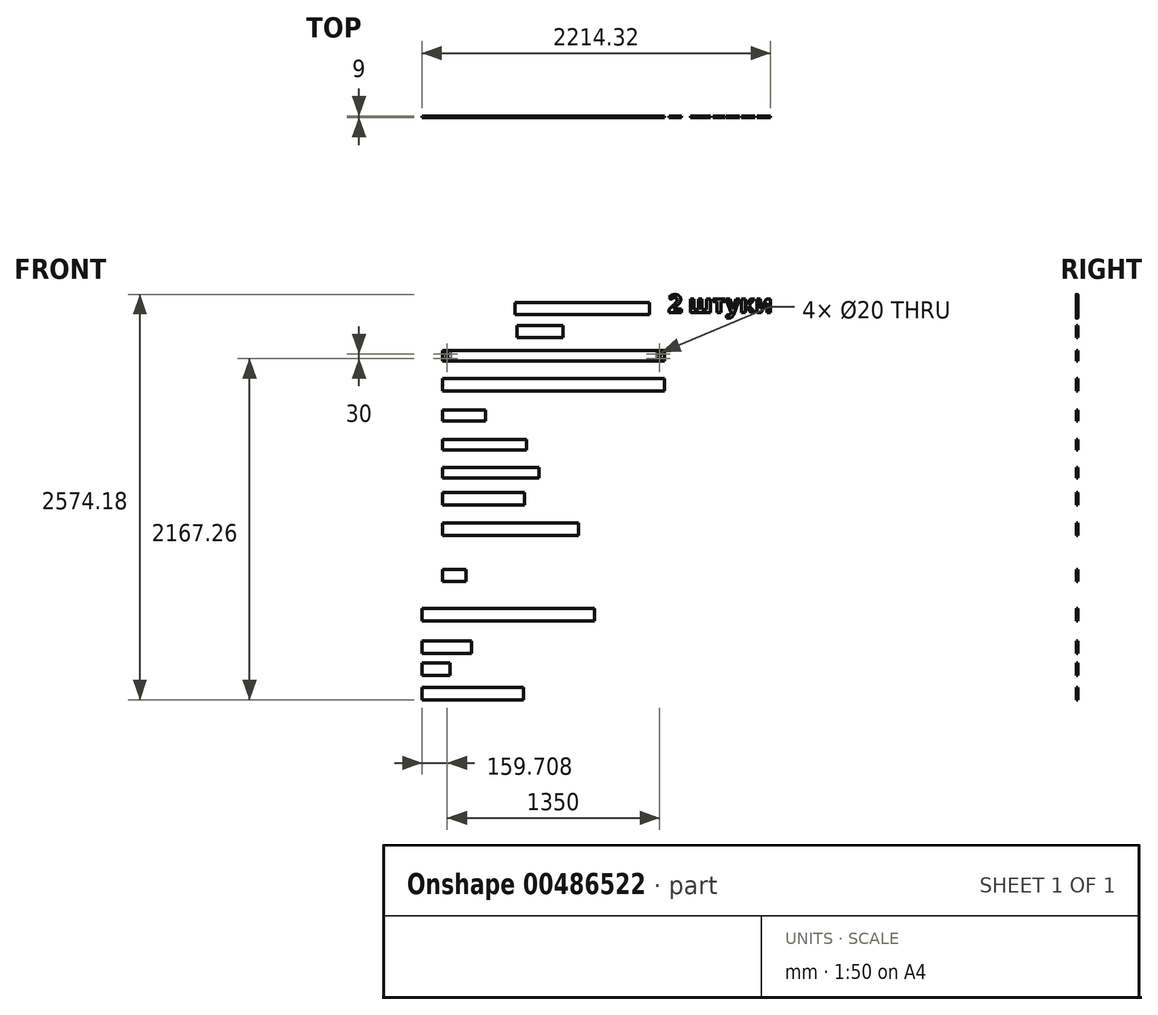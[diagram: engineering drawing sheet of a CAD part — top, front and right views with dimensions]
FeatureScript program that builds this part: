
annotation { "Feature Type Name" : "Feature", "Feature Type Description" : "" }
export const myFeature = defineFeature(function(context is Context, id is Id, definition is map)
    precondition{}
    {
        {
            var Q0;
            Q0=qCreatedBy(makeId("Front.planeOp"),FACE);
            var sketch = newSketch(context, id + "F0", { "sketchPlane" : qUnion([Q0])});
            skLineSegment(sketch, "E0.bottom", {"start": v(-789.19, 96.08) * mm, "end": v(63.81, 96.08) * mm});
            skLineSegment(sketch, "E0.top", {"start": v(-789.19, 18.08) * mm, "end": v(63.81, 18.08) * mm});
            skLineSegment(sketch, "E0.left", {"start": v(-789.19, 96.08) * mm, "end": v(-789.19, 18.08) * mm});
            skLineSegment(sketch, "E0.right", {"start": v(63.81, 96.08) * mm, "end": v(63.81, 18.08) * mm});
            skLineSegment(sketch, "E1.bottom", {"start": v(-776.91, -50.79) * mm, "end": v(-483.91, -50.79) * mm});
            skLineSegment(sketch, "E1.top", {"start": v(-776.91, -128.79) * mm, "end": v(-483.91, -128.79) * mm});
            skLineSegment(sketch, "E1.left", {"start": v(-776.91, -50.79) * mm, "end": v(-776.91, -128.79) * mm});
            skLineSegment(sketch, "E1.right", {"start": v(-483.91, -50.79) * mm, "end": v(-483.91, -128.79) * mm});
            skLineSegment(sketch, "E2.bottom", {"start": v(-1250.2, -211.61) * mm, "end": v(159.8, -211.61) * mm});
            skLineSegment(sketch, "E2.top", {"start": v(-1250.2, -276.61) * mm, "end": v(159.8, -276.61) * mm});
            skLineSegment(sketch, "E2.left", {"start": v(-1250.2, -211.61) * mm, "end": v(-1250.2, -276.61) * mm});
            skLineSegment(sketch, "E2.right", {"start": v(159.8, -211.61) * mm, "end": v(159.8, -276.61) * mm});
            skLineSegment(sketch, "E3.bottom", {"start": v(-1250.2, -388.95) * mm, "end": v(159.8, -388.95) * mm});
            skLineSegment(sketch, "E3.top", {"start": v(-1250.2, -465.95) * mm, "end": v(159.8, -465.95) * mm});
            skLineSegment(sketch, "E3.left", {"start": v(-1250.2, -388.95) * mm, "end": v(-1250.2, -465.95) * mm});
            skLineSegment(sketch, "E3.right", {"start": v(159.8, -388.95) * mm, "end": v(159.8, -465.95) * mm});
            skLineSegment(sketch, "E4", {"start": v(-1196.2, -211.61) * mm, "end": v(-1196.2, -276.61) * mm});
            skCircle(sketch, "E5", {"center": v(-1220.2, -231.61) * mm, "radius": 10 * mm});
            skCircle(sketch, "E6", {"center": v(-1220.2, -261.61) * mm, "radius": 10 * mm});
            skLineSegment(sketch, "E7", {"start": v(105.8, -211.61) * mm, "end": v(105.8, -276.61) * mm});
            skCircle(sketch, "E8", {"center": v(129.8, -231.61) * mm, "radius": 10 * mm});
            skCircle(sketch, "E9", {"center": v(129.8, -261.61) * mm, "radius": 10 * mm});
            skLineSegment(sketch, "E10.bottom", {"start": v(-1250.2, -589.65) * mm, "end": v(-975.2, -589.65) * mm});
            skLineSegment(sketch, "E10.top", {"start": v(-1250.2, -658.65) * mm, "end": v(-975.2, -658.65) * mm});
            skLineSegment(sketch, "E10.left", {"start": v(-1250.2, -589.65) * mm, "end": v(-1250.2, -658.65) * mm});
            skLineSegment(sketch, "E10.right", {"start": v(-975.2, -589.65) * mm, "end": v(-975.2, -658.65) * mm});
            skLineSegment(sketch, "E11.bottom", {"start": v(-1250.2, -774.1) * mm, "end": v(-715.2, -774.1) * mm});
            skLineSegment(sketch, "E11.top", {"start": v(-1250.2, -843.1) * mm, "end": v(-715.2, -843.1) * mm});
            skLineSegment(sketch, "E11.left", {"start": v(-1250.2, -774.1) * mm, "end": v(-1250.2, -843.1) * mm});
            skLineSegment(sketch, "E11.right", {"start": v(-715.2, -774.1) * mm, "end": v(-715.2, -843.1) * mm});
            skLineSegment(sketch, "E12.bottom", {"start": v(-1250.2, -951.78) * mm, "end": v(-637.2, -951.78) * mm});
            skLineSegment(sketch, "E12.top", {"start": v(-1250.2, -1020.78) * mm, "end": v(-637.2, -1020.78) * mm});
            skLineSegment(sketch, "E12.left", {"start": v(-1250.2, -951.78) * mm, "end": v(-1250.2, -1020.78) * mm});
            skLineSegment(sketch, "E12.right", {"start": v(-637.2, -951.78) * mm, "end": v(-637.2, -1020.78) * mm});
            skLineSegment(sketch, "E13.bottom", {"start": v(-1250.2, -1112.74) * mm, "end": v(-730.2, -1112.74) * mm});
            skLineSegment(sketch, "E13.top", {"start": v(-1250.2, -1190.74) * mm, "end": v(-730.2, -1190.74) * mm});
            skLineSegment(sketch, "E13.left", {"start": v(-1250.2, -1112.74) * mm, "end": v(-1250.2, -1190.74) * mm});
            skLineSegment(sketch, "E13.right", {"start": v(-730.2, -1112.74) * mm, "end": v(-730.2, -1190.74) * mm});
            skLineSegment(sketch, "E14.bottom", {"start": v(-1250.2, -1305.86) * mm, "end": v(-385.2, -1305.86) * mm});
            skLineSegment(sketch, "E14.top", {"start": v(-1250.2, -1383.86) * mm, "end": v(-385.2, -1383.86) * mm});
            skLineSegment(sketch, "E14.left", {"start": v(-1250.2, -1305.86) * mm, "end": v(-1250.2, -1383.86) * mm});
            skLineSegment(sketch, "E14.right", {"start": v(-385.2, -1305.86) * mm, "end": v(-385.2, -1383.86) * mm});
            skLineSegment(sketch, "E15.bottom", {"start": v(-1250.2, -1599.41) * mm, "end": v(-1099.2, -1599.41) * mm});
            skLineSegment(sketch, "E15.top", {"start": v(-1250.2, -1677.41) * mm, "end": v(-1099.2, -1677.41) * mm});
            skLineSegment(sketch, "E15.left", {"start": v(-1250.2, -1599.41) * mm, "end": v(-1250.2, -1677.41) * mm});
            skLineSegment(sketch, "E15.right", {"start": v(-1099.2, -1599.41) * mm, "end": v(-1099.2, -1677.41) * mm});
            skLineSegment(sketch, "E16.bottom", {"start": v(-1379.9, -1848.99) * mm, "end": v(-284.9, -1848.99) * mm});
            skLineSegment(sketch, "E16.top", {"start": v(-1379.9, -1926.99) * mm, "end": v(-284.9, -1926.99) * mm});
            skLineSegment(sketch, "E16.left", {"start": v(-1379.9, -1848.99) * mm, "end": v(-1379.9, -1926.99) * mm});
            skLineSegment(sketch, "E16.right", {"start": v(-284.9, -1848.99) * mm, "end": v(-284.9, -1926.99) * mm});
            skLineSegment(sketch, "E17.bottom", {"start": v(-1379.9, -2056.33) * mm, "end": v(-1066.9, -2056.33) * mm});
            skLineSegment(sketch, "E17.top", {"start": v(-1379.9, -2134.33) * mm, "end": v(-1066.9, -2134.33) * mm});
            skLineSegment(sketch, "E17.left", {"start": v(-1379.9, -2056.33) * mm, "end": v(-1379.9, -2134.33) * mm});
            skLineSegment(sketch, "E17.right", {"start": v(-1066.9, -2056.33) * mm, "end": v(-1066.9, -2134.33) * mm});
            skLineSegment(sketch, "E18.bottom", {"start": v(-1379.9, -2196.25) * mm, "end": v(-1202.9, -2196.25) * mm});
            skLineSegment(sketch, "E18.top", {"start": v(-1379.9, -2274.25) * mm, "end": v(-1202.9, -2274.25) * mm});
            skLineSegment(sketch, "E18.left", {"start": v(-1379.9, -2196.25) * mm, "end": v(-1379.9, -2274.25) * mm});
            skLineSegment(sketch, "E18.right", {"start": v(-1202.9, -2196.25) * mm, "end": v(-1202.9, -2274.25) * mm});
            skLineSegment(sketch, "E19.bottom", {"start": v(-1379.9, -2350.87) * mm, "end": v(-733.9, -2350.87) * mm});
            skLineSegment(sketch, "E19.top", {"start": v(-1379.9, -2428.87) * mm, "end": v(-733.9, -2428.87) * mm});
            skLineSegment(sketch, "E19.left", {"start": v(-1379.9, -2350.87) * mm, "end": v(-1379.9, -2428.87) * mm});
            skLineSegment(sketch, "E19.right", {"start": v(-733.9, -2350.87) * mm, "end": v(-733.9, -2428.87) * mm});
            skText(sketch, "E20", { "text": "2 штуки", "fontName": "OpenSans-Bold.ttf"});
            const initialGuessF0  = {"E20": [0.18252, 0.03248, 1, 0, 0.1122]};
            skSetInitialGuess(sketch, initialGuessF0);
            skSolve(sketch);
        }
        {
            var Q0;
            Q0 = qSketchRegion(id + "F0", true);
            extrude(context, id + "F1", {"entities" : qUnion([Q0]), "depth" : 9 * mm, "offsetDistance" : 25 * mm});
        }
        {
            var Q0;
            {var subQ1=sQuery(id+"F0.wireOp",EDGE,"E2.left");Q0=makeQuery(id+"F0.imprint","IMPRINT",FACE,{"disambiguationData":[TD([[makeQuery(id+"F0.imprint","IMPRINT",EDGE,{"derivedFrom":subQ1}),1.0]])]});}
            var Q1;
            {var subQ1=sQuery(id+"F0.wireOp",EDGE,"E2.right");Q1=makeQuery(id+"F0.imprint","IMPRINT",FACE,{"disambiguationData":[TD([[makeQuery(id+"F0.imprint","IMPRINT",EDGE,{"derivedFrom":subQ1}),-1.0]])]});}
            extrude(context, id + "F2", {"entities" : qUnion([Q0, Q1]), "operationType" : NewBodyOperationType.REMOVE, "depth" : 5 * mm, "offsetDistance" : 25 * mm});
        }
    });
